# Revit family: EKF_EE_КомплектДверейFORT_IP31_PROxima
name_source: partatom
category: Электрооборудование
units: mm (PartAtom-declared; Revit-internal decimal feet)

## family parameters
Всегда вертикально = Нет
На основе рабочей плоскости = Да
Общий = Да
При загрузке вырезать с полостями = Нет
Размер круглого соединителя = Использовать диаметр
Тип детали = Силовой щит
Точка расчета площади = Нет

## types (3) — shared parameters
ADSK_Единица измерения = шт.
ADSK_Завод-изготовитель = EKF
ADSK_Количество = 1
ADSK_Марка = Комплект дверей FORT
ADSK_Материал = RAL 7035_Сталь
ADSK_Обозначение = Комплект дверей FORT
ADSK_Размер_Глубина = 21 мм
ADSK_Размер_Ширина = 987 мм
Изготовитель = EKF
Карман для документации = Да
КолОтв = 4
Серия номенклатуры = PROxima
Степень защиты IP = IP31
ТВ = EKF_2
Тип установки = -
Ширина = 491.5 мм
zero-valued in all types: ADSK_Масса, Отметка по умолчанию

## per-type parameters (varying)
| type | ADSK_Код изделия | ADSK_Размер_Высота | Тип |
| Комплект дверей FORT для корпуса высотой 1800 и шириной 1000 IP31 EKF PROxima | FD1810 | 1800 мм | 388 мм |
| Комплект дверей FORT для корпуса высотой 2000 и шириной 1000 IP31 EKF PROxima | FD2010 | 2000 мм | 390 мм |
| Комплект дверей FORT для корпуса высотой 2200 и шириной 1000 IP31 EKF PROxima | FD2210 | 2200 мм | 392 мм |

note: column(s) folded — value = type name in every type: ADSK_Наименование
